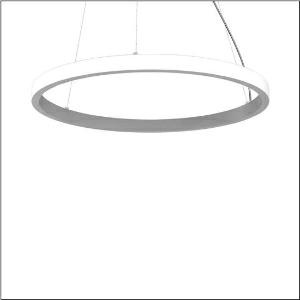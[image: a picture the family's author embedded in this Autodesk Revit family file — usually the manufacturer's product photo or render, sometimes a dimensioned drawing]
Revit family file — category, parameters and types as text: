
# Revit family: silica_r__21_ring-o_5pjbo4d1204a_97b4
name_source: partatom
category: Lighting Fixtures
units: mm (PartAtom-declared; Revit-internal decimal feet)

## family parameters
Cut with Voids When Loaded = No
Host = Face
Light Source = No
Part Type = Normal
Room Calculation Point = No
Round Connector Dimension = Use Diameter
Shared = No

## types (1)
- Silica® 21 Ring-O (1 x LED, 8820 lm, 343 W, 3000K)
    Apparent Load = 343 VA
    CIE Flux Codes = 2 16 49 50 100
    Color Rendering = 80
    Color Temperature = 3000K
    Default Elevation = 1800 mm
    Description = Silica® 21 Ring-O, suspended luminaire, of PMMA, frosted, light emission: outer ring side luminous distribution, primary light characteristic: symmetric, installation type: suspended mounting, LED, rated luminous flux: 8.820lm, luminous efficacy: 63lm/W, light colour: 830, colour temperature: 3000K, with terminal, 5-pole, mains connection: 230V, AC/DC, 0/50..60Hz, rated input power: 140W, housing, of extruded aluminium section, metallic grey (RAL 9006), diameter: 1.480mm, ceiling canopy, metallic grey (RAL 9006), protection rating (lamp compartment): IP40, insulation class (complete): insulation class I (protective earthing), certification: CE, impact resistance: IK02, permissible operating ambient temperature: 0..+35°C, packaging unit: 1 piece
    Height = 48 mm
    Lamp = 1 x LED
    Lamp Light Flux = 8820 lm
    Lamp Power = 343 W
    Lamp count = 1
    Length = 1480 mm
    Luminous efficacy = 26 lm/W
    Manufacturer = Siteco
    ModVariant = No
    Model = 5PJBO4D1204A
    Mounting Place = Ceiling
    Mounting Type = Pendant
    Number of Poles = 1
    OnlyDefault = Yes
    Power Factor = 1
    Product Name = Silica® 21 Ring-O
    Product group = suspended luminaire
    ProductGroupID = 904
    Protection Class = Protection class I
    Protection Degree = Degree of protection
    RLX_Detail_Level = 1
    RLX_Emergency_Light_Flux = 0 lm
    RLX_Emergency_Type = 0
    RLX_Emergency_Type_DB = No
    RlxData = <blob elided: 18393 chars, md5=3f36de18>
    Socket = socket
    Standby Power = 0 W
    System Light Flux = 8819 lm
    System Power = 343 W
    Type Comments = Product without accessories
    Type Image = l_1251764.jpg
    URL = http://relux.com
    VarID = ---
    Voltage = 0 V
    Weight = 0.00 kg
    Width = 0 mm  [stored 0 ft]

note: [stored X ft] marks values corroborated as IEEE doubles in the binary element streams (Revit-internal decimal feet)

## geometry (parser evidence)
native form markers: Blend x4, Sweep x14
no freeform markers — native parametric forms only
